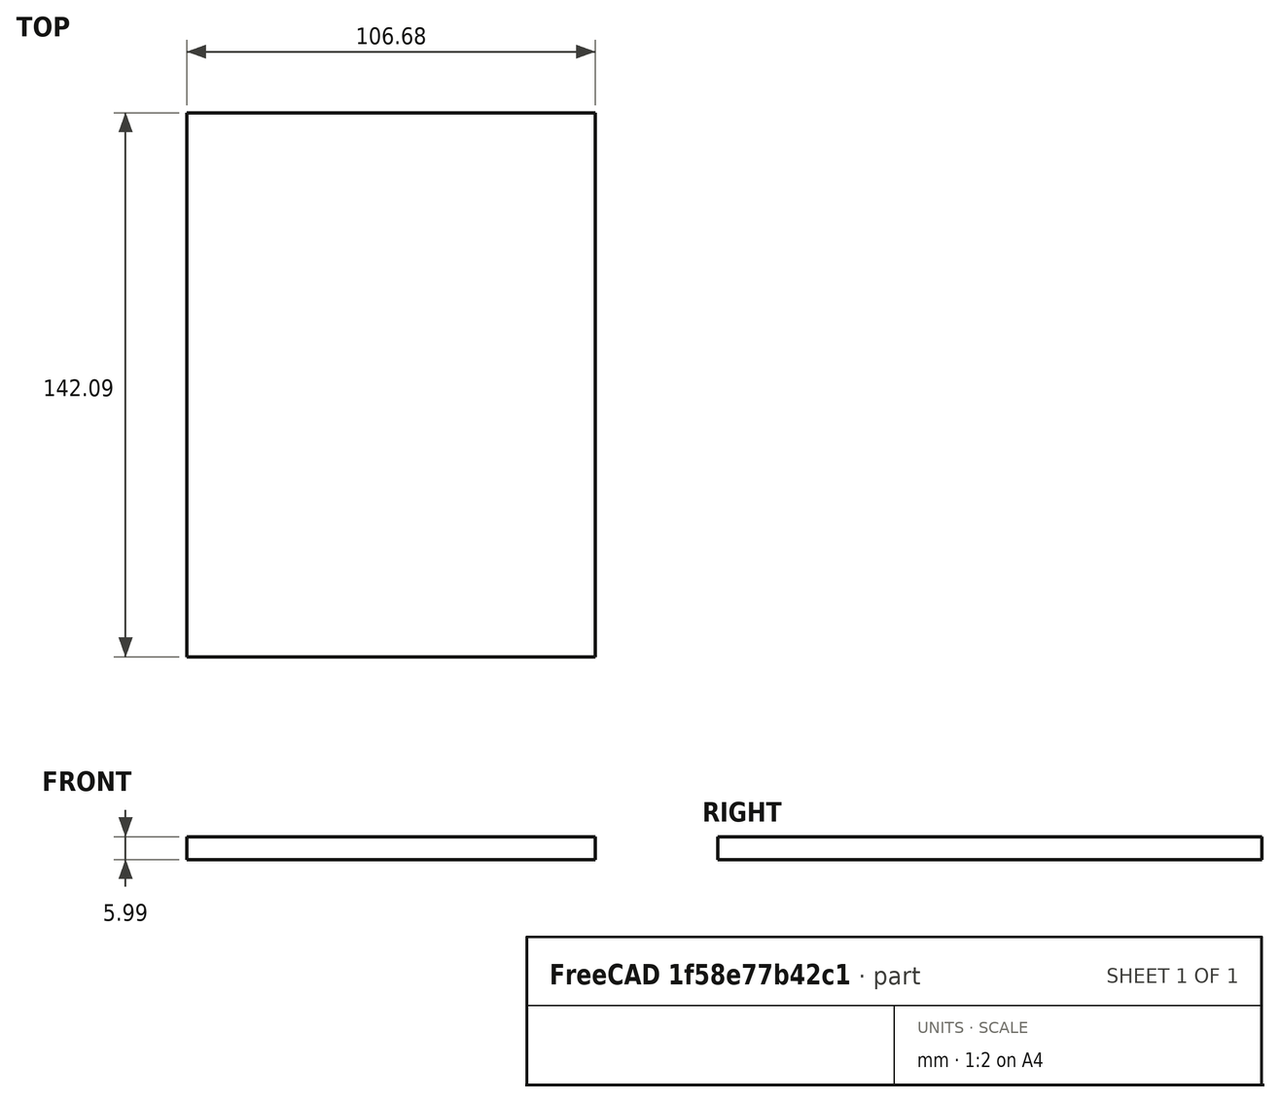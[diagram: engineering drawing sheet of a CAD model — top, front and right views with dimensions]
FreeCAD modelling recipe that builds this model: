
FCSTD DOCUMENT  (FreeCAD 0.19R24267 (Git))
Label: Inv1-P10
License: All rights reserved
LicenseURL: http://en.wikipedia.org/wiki/All_rights_reserved
objects: TechDraw::DrawViewDimension×3, TechDraw::DrawProjGroupItem×2, TechDraw::DrawHatch×2, TechDraw::DrawViewAnnotation×2, Sketcher::SketchObject×1, Part::Extrusion×1, TechDraw::DrawSVGTemplate×1, TechDraw::DrawProjGroup×1, TechDraw::DrawPage×1
note: 2 computed .brp shape members not serialized (recipe doc carries the construction recipe); baked Part::Feature solids carry a one-line shape summary decoded from their .brp

FEATURE [Sketcher::SketchObject] Sketch
  FullyConstrained = false
  sketch-geometry (4):
    g0: LineSegment StartX=-46.2205 StartY=54.0154 StartZ=0 EndX=60.4595 EndY=54.0154 EndZ=0
    g1: LineSegment StartX=60.4595 StartY=54.0154 StartZ=0 EndX=60.4595 EndY=-88.0722 EndZ=0
    g2: LineSegment StartX=60.4595 StartY=-88.0722 StartZ=0 EndX=-46.2205 EndY=-88.0722 EndZ=0
    g3: LineSegment StartX=-46.2205 StartY=-88.0722 StartZ=0 EndX=-46.2205 EndY=54.0154 EndZ=0
  constraints (10):
    c: Coincident(g0,g1)
    c: Coincident(g1,g2)
    c: Coincident(g2,g3)
    c: Coincident(g3,g0)
    c: Horizontal(g0)
    c: Horizontal(g2)
    c: Vertical(g1)
    c: Vertical(g3)
    c: DistanceX(g0,g0) = 106.68
    c: DistanceY(g3,g3) = 142.088
FEATURE [Part::Extrusion] Extrude
  Base = -> Sketch
  Dir = (0,0,1)
  DirMode = 2
  FaceMakerClass = Part::FaceMakerBullseye
  LengthFwd = 5.9944
  LengthRev = 0
  Solid = true
  Symmetric = false
FEATURE [TechDraw::DrawSVGTemplate] Template
  Height = 215.9
  Orientation = 1
  Width = 279.4
FEATURE [TechDraw::DrawProjGroupItem] ProjItem  label="Front"
  CoarseView = false
  Direction = (0,0,1)
  Focus = 100
  HardHidden = false
  IsoCount = 0
  IsoHidden = false
  IsoVisible = false
  LockPosition = true
  Perspective = false
  Rotation = 0
  RotationVector = (0,1,0)
  Scale = 0.5
  ScaleType = 2
  SeamHidden = false
  SeamVisible = true
  SmoothHidden = false
  SmoothVisible = true
  Source = -> [Extrude]
  Type = 0
  X = 0
  XDirection = (0,1,0)
  Y = 0
FEATURE [TechDraw::DrawProjGroupItem] ProjItem001  label="Left"
  CoarseView = false
  Direction = (0,-1,1e-16)
  Focus = 100
  HardHidden = false
  IsoCount = 0
  IsoHidden = false
  IsoVisible = false
  LockPosition = false
  Perspective = false
  Rotation = 0
  RotationVector = (1,0,0)
  ScaleType = 2
  SeamHidden = false
  SeamVisible = true
  SmoothHidden = false
  SmoothVisible = true
  Source = -> [Extrude]
  Type = 1
  X = 74.6571
  XDirection = (0,1e-16,1)
  Y = 0
FEATURE [TechDraw::DrawProjGroup] ProjGroup
  Anchor = -> ProjItem
  AutoDistribute = true
  LockPosition = false
  ProjectionType = 0
  Rotation = 0
  Scale = 0.5
  ScaleType = 2
  Source = -> [Extrude]
  Views = -> [ProjItem,ProjItem001]
  X = 118.275
  Y = 105.403
  spacingX = 15.0114
  spacingY = 15.0114
FEATURE [TechDraw::DrawHatch] Hatch  label="HatchF0"
  HatchPattern = <path>
  Source = -> ProjItem [Face0]
FEATURE [TechDraw::DrawHatch] Hatch001  label="Hatch001F0"
  HatchPattern = <path>
  Source = -> ProjItem001 [Face0]
FEATURE [TechDraw::DrawViewDimension] Dimension
  Arbitrary = false
  ArbitraryTolerances = false
  EqualTolerance = true
  FormatSpec = %.3f
  FormatSpecOverTolerance = %+.3f
  FormatSpecUnderTolerance = %+.3f
  Inverted = false
  LockPosition = false
  MeasureType = 1
  OverTolerance = 0
  References2D = -> [ProjItem]
  Rotation = 0
  ScaleType = 0
  TheoreticalExact = false
  Type = 2
  UnderTolerance = 0
  X = 45.5258
  Y = 0.638546
FEATURE [TechDraw::DrawViewDimension] Dimension001
  Arbitrary = false
  ArbitraryTolerances = false
  EqualTolerance = true
  FormatSpec = %.3f
  FormatSpecOverTolerance = %+.3f
  FormatSpecUnderTolerance = %+.3f
  Inverted = false
  LockPosition = false
  MeasureType = 1
  OverTolerance = 0
  References2D = -> [ProjItem]
  Rotation = 0
  ScaleType = 0
  TheoreticalExact = false
  Type = 1
  UnderTolerance = 0
  X = 1.70279
  Y = -38.5895
FEATURE [TechDraw::DrawViewDimension] Dimension002
  Arbitrary = false
  ArbitraryTolerances = false
  EqualTolerance = true
  FormatSpec = %.3f
  FormatSpecOverTolerance = %+.3f
  FormatSpecUnderTolerance = %+.3f
  Inverted = false
  LockPosition = false
  MeasureType = 1
  OverTolerance = 0
  References2D = -> [ProjItem001]
  Rotation = 0
  ScaleType = 0
  TheoreticalExact = false
  Type = 1
  UnderTolerance = 0
  X = 23.839
  Y = 15.1762
FEATURE [TechDraw::DrawViewAnnotation] Annotation
  Font = osifont
  LineSpace = 80
  LockPosition = false
  MaxWidth = -1
  Rotation = 0
  ScaleType = 0
  Text = Figure S1 (Inverted 1) | Panel 10 [focus knob top back] | Quantity: 1
  TextSize = 5.0038
  TextStyle = 0
  X = 43.0359
  Y = 195.58
FEATURE [TechDraw::DrawViewAnnotation] Annotation002
  Font = osifont
  LineSpace = 80
  LockPosition = false
  MaxWidth = -1
  Rotation = 0
  ScaleType = 0
  Text = Units: Inches
  TextSize = 5.0038
  TextStyle = 0
  X = 259.08
  Y = 5.08
FEATURE [TechDraw::DrawPage] Page
  KeepUpdated = true
  NextBalloonIndex = 1
  ProjectionType = 0
  Template = -> Template
  Views = -> [ProjGroup,Dimension,Dimension001,Dimension002,Annotation,Annotation002]
note: 2 file-system paths scrubbed to <path> (originals preserved in the JSON sidecar)
